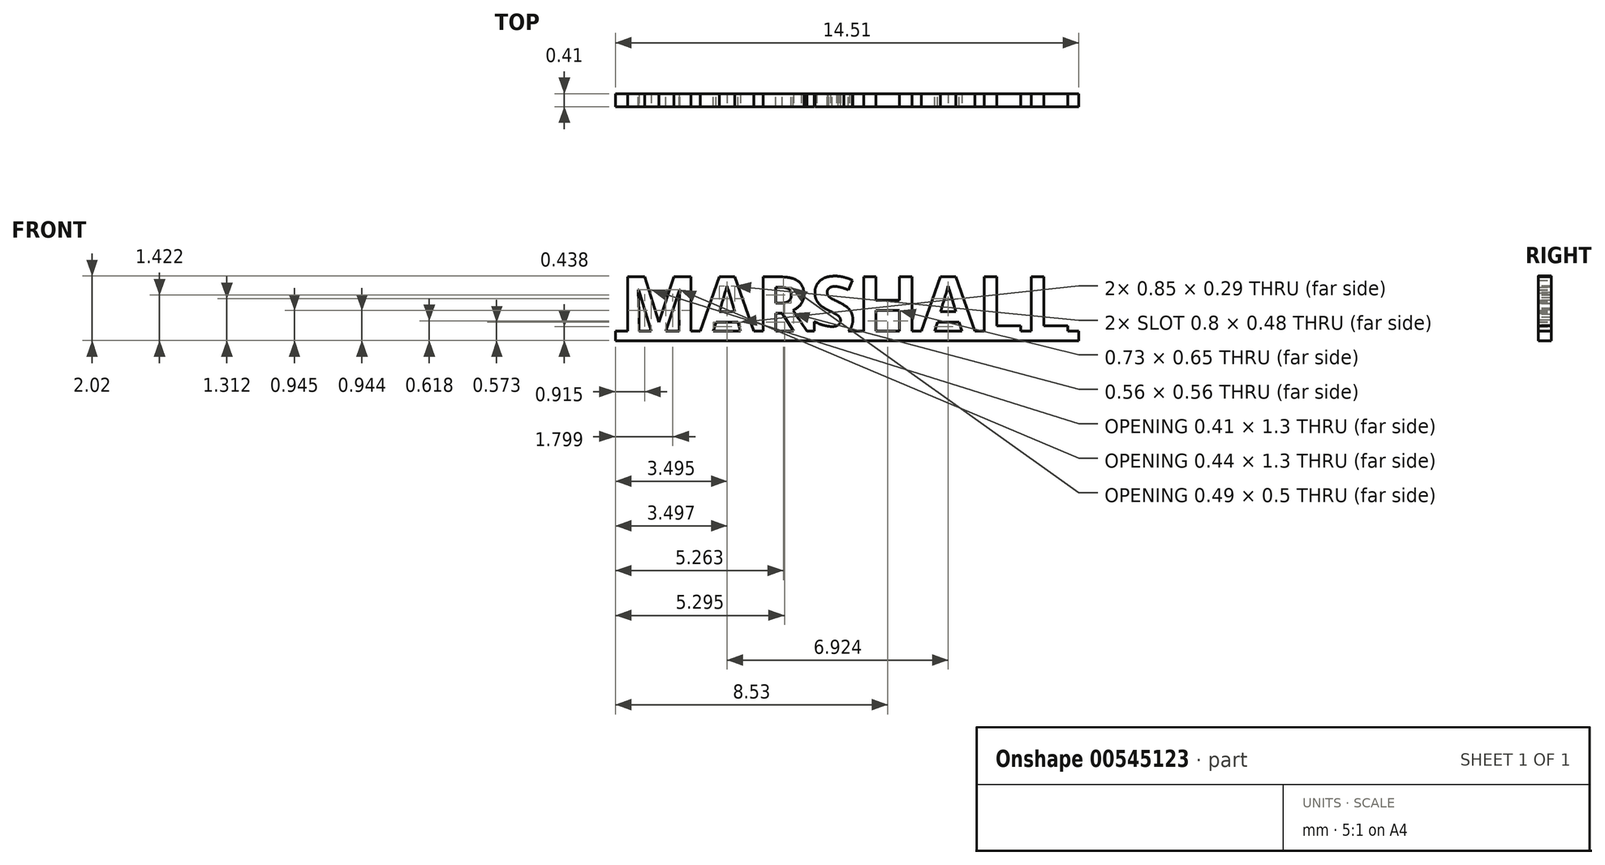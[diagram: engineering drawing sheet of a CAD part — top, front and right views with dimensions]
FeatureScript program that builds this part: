
annotation { "Feature Type Name" : "Feature", "Feature Type Description" : "" }
export const myFeature = defineFeature(function(context is Context, id is Id, definition is map)
    precondition{}
    {
        {
            var Q0;
            Q0=qCreatedBy(makeId("Front.planeOp"),FACE);
            var sketch = newSketch(context, id + "F0", { "sketchPlane" : qUnion([Q0])});
            skText(sketch, "E0", { "text": "MARSHALL", "fontName": "OpenSans-Bold.ttf"});
            const initialGuessF0  = {"E0": [-0.00976, 0, 1, 0, 0.00187]};
            skSetInitialGuess(sketch, initialGuessF0);
            skSolve(sketch);
        }
        {
            var Q0;
            Q0=qCreatedBy(makeId("Front.planeOp"),FACE);
            var sketch = newSketch(context, id + "F1", { "sketchPlane" : qUnion([Q0])});
            skLineSegment(sketch, "E1.bottom", {"start": v(-9.9, 0.16) * mm, "end": v(4.6, 0.16) * mm});
            skLineSegment(sketch, "E1.top", {"start": v(-9.9, -0.14) * mm, "end": v(4.6, -0.14) * mm});
            skLineSegment(sketch, "E1.left", {"start": v(-9.9, 0.16) * mm, "end": v(-9.9, -0.14) * mm});
            skLineSegment(sketch, "E1.right", {"start": v(4.6, 0.16) * mm, "end": v(4.6, -0.14) * mm});
            skSolve(sketch);
        }
        {
            var Q0;
            Q0 = qSketchRegion(id + "F1", true);
            extrude(context, id + "F2", {"entities" : qUnion([Q0]), "depth" : 0.4 * mm, "offsetDistance" : 25.4 * mm});
        }
        {
            var Q0;
            Q0 = qSketchRegion(id + "F0", true);
            extrude(context, id + "F3", {"entities" : qUnion([Q0]), "operationType" : NewBodyOperationType.ADD, "depth" : 0.4 * mm, "offsetDistance" : 25.4 * mm});
        }
    });
